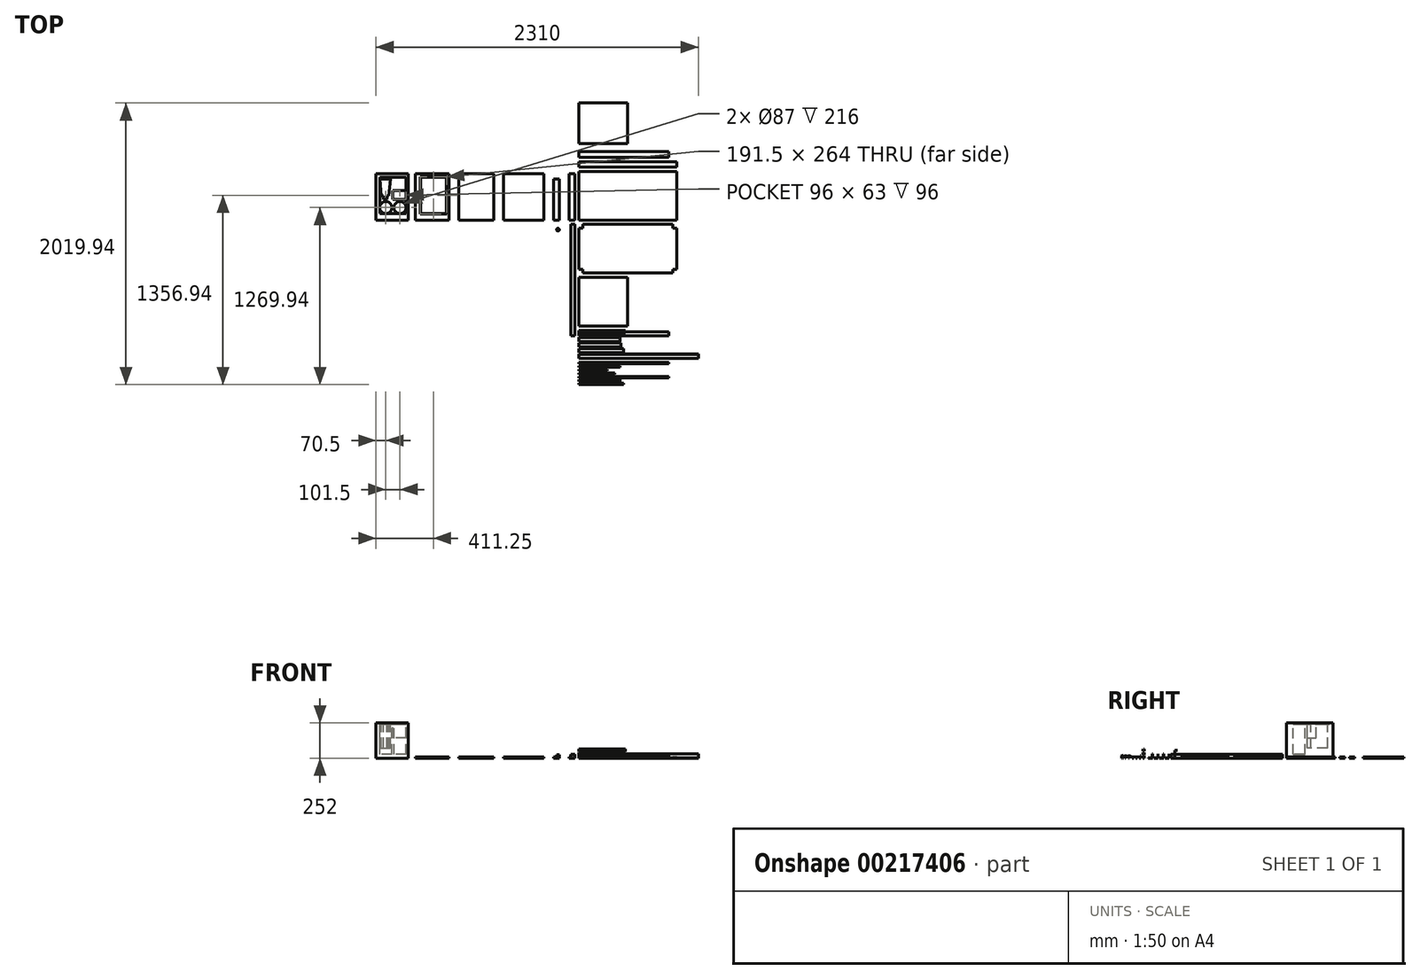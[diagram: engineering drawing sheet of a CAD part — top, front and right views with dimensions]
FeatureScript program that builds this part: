
annotation { "Feature Type Name" : "Feature", "Feature Type Description" : "" }
export const myFeature = defineFeature(function(context is Context, id is Id, definition is map)
    precondition{}
    {
        {
            assignVariable(context, id + "F0", {"name" : "length", "anyValue" : 700});
        }
        {
            assignVariable(context, id + "F1", {"name" : "width", "anyValue" : 350});
        }
        {
            assignVariable(context, id + "F2", {"name" : "height", "anyValue" : 800});
        }
        {
            assignVariable(context, id + "F3", {"name" : "panelW", "anyValue" : 8});
        }
        {
            assignVariable(context, id + "F4", {"name" : "postW", "anyValue" : 28});
        }
        {
            assignVariable(context, id + "F5", {"name" : "shelfH", "anyValue" : 40});
        }
        {
            assignVariable(context, id + "F6", {"name" : "profileW", "anyValue" : 1.5});
        }
        {
            assignVariable(context, id + "F7", {"name" : "topH", "anyValue" : 290});
        }
        {
            var Q0;
            Q0=qCreatedBy(makeId("Top.planeOp"),FACE);
            var sketch = newSketch(context, id + "F8", { "sketchPlane" : qUnion([Q0])});
            skLineSegment(sketch, "E0.bottom", {"start": v(0, 0) * mm, "end": v(700, 0) * mm});
            skLineSegment(sketch, "E0.top", {"start": v(0, 350) * mm, "end": v(700, 350) * mm});
            skLineSegment(sketch, "E0.left", {"start": v(0, 0) * mm, "end": v(0, 350) * mm});
            skLineSegment(sketch, "E0.right", {"start": v(700, 0) * mm, "end": v(700, 350) * mm});
            skLineSegment(sketch, "E1.bottom", {"start": v(0, 380) * mm, "end": v(700, 380) * mm});
            skLineSegment(sketch, "E1.top", {"start": v(0, 420) * mm, "end": v(700, 420) * mm});
            skLineSegment(sketch, "E1.left", {"start": v(0, 380) * mm, "end": v(0, 420) * mm});
            skLineSegment(sketch, "E1.right", {"start": v(700, 380) * mm, "end": v(700, 420) * mm});
            skLineSegment(sketch, "E2.bottom", {"start": v(-30, 0) * mm, "end": v(-70, 0) * mm});
            skLineSegment(sketch, "E2.top", {"start": v(-30, 334) * mm, "end": v(-70, 334) * mm});
            skLineSegment(sketch, "E2.left", {"start": v(-30, 0) * mm, "end": v(-30, 334) * mm});
            skLineSegment(sketch, "E2.right", {"start": v(-70, 0) * mm, "end": v(-70, 334) * mm});
            skLineSegment(sketch, "E3.bottom", {"start": v(0, 450) * mm, "end": v(644, 450) * mm});
            skLineSegment(sketch, "E3.top", {"start": v(0, 490) * mm, "end": v(644, 490) * mm});
            skLineSegment(sketch, "E3.left", {"start": v(0, 450) * mm, "end": v(0, 490) * mm});
            skLineSegment(sketch, "E3.right", {"start": v(644, 450) * mm, "end": v(644, 490) * mm});
            skLineSegment(sketch, "E4.bottom", {"start": v(-140, 0) * mm, "end": v(-180, 0) * mm});
            skLineSegment(sketch, "E4.top", {"start": v(-140, 294) * mm, "end": v(-180, 294) * mm});
            skLineSegment(sketch, "E4.left", {"start": v(-140, 0) * mm, "end": v(-140, 294) * mm});
            skLineSegment(sketch, "E4.right", {"start": v(-180, 0) * mm, "end": v(-180, 294) * mm});
            skLineSegment(sketch, "E5.bottom", {"start": v(28, -30) * mm, "end": v(672, -30) * mm});
            skLineSegment(sketch, "E5.top", {"start": v(28, -380) * mm, "end": v(672, -380) * mm});
            skLineSegment(sketch, "E5.left", {"start": v(0, -58) * mm, "end": v(0, -352) * mm});
            skLineSegment(sketch, "E5.right", {"start": v(700, -58) * mm, "end": v(700, -352) * mm});
            skLineSegment(sketch, "E6", {"start": v(0, -58) * mm, "end": v(28, -58) * mm});
            skLineSegment(sketch, "E7", {"start": v(28, -58) * mm, "end": v(28, -30) * mm});
            skLineSegment(sketch, "E8", {"start": v(350, -30) * mm, "end": v(350, -380) * mm, "construction": true});
            skLineSegment(sketch, "E9", {"start": v(0, -205) * mm, "end": v(700, -205) * mm, "construction": true});
            skPoint(sketch, "E10.orphan", {"position": v(0, -30) * mm});
            skLineSegment(sketch, "E11.MirrorCS", {"start": v(700, -58) * mm, "end": v(672, -58) * mm});
            skLineSegment(sketch, "E12.MirrorCS", {"start": v(672, -58) * mm, "end": v(672, -30) * mm});
            skPoint(sketch, "E13.MirrorP", {"position": v(700, -30) * mm});
            skLineSegment(sketch, "E14.MirrorCS", {"start": v(0, -352) * mm, "end": v(28, -352) * mm});
            skLineSegment(sketch, "E15.MirrorCS", {"start": v(28, -352) * mm, "end": v(28, -380) * mm});
            skLineSegment(sketch, "E16.MirrorCS", {"start": v(672, -352) * mm, "end": v(672, -380) * mm});
            skLineSegment(sketch, "E17.MirrorCS", {"start": v(700, -352) * mm, "end": v(672, -352) * mm});
            skPoint(sketch, "E18.orphan", {"position": v(700, -380) * mm});
            skPoint(sketch, "E19.orphan", {"position": v(0, -380) * mm});
            skPoint(sketch, "E20.oppositeSnap0", {"position": v(-50, 334) * mm});
            skLineSegment(sketch, "E20.bottom", {"start": v(-250, 0) * mm, "end": v(-540, 0) * mm});
            skLineSegment(sketch, "E20.top", {"start": v(-250, 334) * mm, "end": v(-540, 334) * mm});
            skLineSegment(sketch, "E20.left", {"start": v(-250, 0) * mm, "end": v(-250, 334) * mm});
            skLineSegment(sketch, "E20.right", {"start": v(-540, 0) * mm, "end": v(-540, 334) * mm});
            skLineSegment(sketch, "E21.bottom", {"start": v(0, 550) * mm, "end": v(348.5, 550) * mm});
            skLineSegment(sketch, "E21.top", {"start": v(0, 840) * mm, "end": v(348.5, 840) * mm});
            skLineSegment(sketch, "E21.left", {"start": v(0, 550) * mm, "end": v(0, 840) * mm});
            skLineSegment(sketch, "E21.right", {"start": v(348.5, 550) * mm, "end": v(348.5, 840) * mm});
            skLineSegment(sketch, "E22.bottom", {"start": v(0, -410) * mm, "end": v(348.5, -410) * mm});
            skLineSegment(sketch, "E22.top", {"start": v(0, -760) * mm, "end": v(348.5, -760) * mm});
            skLineSegment(sketch, "E22.left", {"start": v(0, -410) * mm, "end": v(0, -760) * mm});
            skLineSegment(sketch, "E22.right", {"start": v(348.5, -410) * mm, "end": v(348.5, -760) * mm});
            skLineSegment(sketch, "E23.bottom", {"start": v(-610, 0) * mm, "end": v(-862, 0) * mm});
            skLineSegment(sketch, "E23.top", {"start": v(-610, 334) * mm, "end": v(-862, 334) * mm});
            skLineSegment(sketch, "E23.left", {"start": v(-610, 0) * mm, "end": v(-610, 334) * mm});
            skLineSegment(sketch, "E23.right", {"start": v(-862, 0) * mm, "end": v(-862, 334) * mm});
            skLineSegment(sketch, "E24.bottom", {"start": v(-932, 0) * mm, "end": v(-1172, 0) * mm});
            skLineSegment(sketch, "E24.top", {"start": v(-932, 334) * mm, "end": v(-1172, 334) * mm});
            skLineSegment(sketch, "E24.left", {"start": v(-932, 0) * mm, "end": v(-932, 334) * mm});
            skLineSegment(sketch, "E24.right", {"start": v(-1172, 0) * mm, "end": v(-1172, 334) * mm});
            skLineSegment(sketch, "E25.bottom", {"start": v(-947, 45) * mm, "end": v(-1138.5, 45) * mm});
            skLineSegment(sketch, "E25.top", {"start": v(-947, 309) * mm, "end": v(-1138.5, 309) * mm});
            skLineSegment(sketch, "E25.left", {"start": v(-947, 45) * mm, "end": v(-947, 309) * mm});
            skLineSegment(sketch, "E25.right", {"start": v(-1138.5, 45) * mm, "end": v(-1138.5, 309) * mm});
            skLineSegment(sketch, "E26.bottom", {"start": v(-1135.5, 306) * mm, "end": v(-950, 306) * mm});
            skLineSegment(sketch, "E26.top", {"start": v(-1135.5, 48) * mm, "end": v(-950, 48) * mm});
            skLineSegment(sketch, "E26.left", {"start": v(-1135.5, 306) * mm, "end": v(-1135.5, 48) * mm});
            skLineSegment(sketch, "E26.right", {"start": v(-950, 306) * mm, "end": v(-950, 48) * mm});
            skSolve(sketch);
        }
        {
            var Q0;
            Q0 = qSketchRegion(id + "F8", true);
            extrude(context, id + "F9", {"entities" : qUnion([Q0]), "depth" : (getVariable(context, 'panelW')) * mm});
        }
        {
            var Q0;
            Q0=qCreatedBy(makeId("Right.planeOp"),FACE);
            var sketch = newSketch(context, id + "F10", { "sketchPlane" : qUnion([Q0])});
            skLineSegment(sketch, "E27", {"start": v(-800, 0) * mm, "end": v(-800, 30) * mm});
            skLineSegment(sketch, "E28", {"start": v(-800, 30) * mm, "end": v(-801.5, 30) * mm});
            skLineSegment(sketch, "E29", {"start": v(-801.5, 30) * mm, "end": v(-801.5, 1.5) * mm});
            skLineSegment(sketch, "E30", {"start": v(-801.5, 1.5) * mm, "end": v(-830, 1.5) * mm});
            skLineSegment(sketch, "E31", {"start": v(-830, 1.5) * mm, "end": v(-830, 0) * mm});
            skLineSegment(sketch, "E32", {"start": v(-830, 0) * mm, "end": v(-800, 0) * mm});
            skLineSegment(sketch, "E33.1.0.0", {"start": v(-870, 0) * mm, "end": v(-840, 0) * mm});
            skLineSegment(sketch, "E33.1.0.1", {"start": v(-840, 0) * mm, "end": v(-840, 30) * mm});
            skLineSegment(sketch, "E33.1.0.2", {"start": v(-841.5, 1.5) * mm, "end": v(-870, 1.5) * mm});
            skLineSegment(sketch, "E33.1.0.3", {"start": v(-841.5, 30) * mm, "end": v(-841.5, 1.5) * mm});
            skLineSegment(sketch, "E33.1.0.4", {"start": v(-840, 30) * mm, "end": v(-841.5, 30) * mm});
            skLineSegment(sketch, "E33.1.0.5", {"start": v(-870, 1.5) * mm, "end": v(-870, 0) * mm});
            skLineSegment(sketch, "E33.2.0.0", {"start": v(-910, 0) * mm, "end": v(-880, 0) * mm});
            skLineSegment(sketch, "E33.2.0.1", {"start": v(-880, 0) * mm, "end": v(-880, 30) * mm});
            skLineSegment(sketch, "E33.2.0.2", {"start": v(-881.5, 1.5) * mm, "end": v(-910, 1.5) * mm});
            skLineSegment(sketch, "E33.2.0.3", {"start": v(-881.5, 30) * mm, "end": v(-881.5, 1.5) * mm});
            skLineSegment(sketch, "E33.2.0.4", {"start": v(-880, 30) * mm, "end": v(-881.5, 30) * mm});
            skLineSegment(sketch, "E33.2.0.5", {"start": v(-910, 1.5) * mm, "end": v(-910, 0) * mm});
            skLineSegment(sketch, "E33.3.0.0", {"start": v(-950, 0) * mm, "end": v(-920, 0) * mm});
            skLineSegment(sketch, "E33.3.0.1", {"start": v(-920, 0) * mm, "end": v(-920, 30) * mm});
            skLineSegment(sketch, "E33.3.0.2", {"start": v(-921.5, 1.5) * mm, "end": v(-950, 1.5) * mm});
            skLineSegment(sketch, "E33.3.0.3", {"start": v(-921.5, 30) * mm, "end": v(-921.5, 1.5) * mm});
            skLineSegment(sketch, "E33.3.0.4", {"start": v(-920, 30) * mm, "end": v(-921.5, 30) * mm});
            skLineSegment(sketch, "E33.3.0.5", {"start": v(-950, 1.5) * mm, "end": v(-950, 0) * mm});
            skLineSegment(sketch, "E33.4.0.0", {"start": v(-990, 0) * mm, "end": v(-960, 0) * mm});
            skLineSegment(sketch, "E33.4.0.1", {"start": v(-960, 0) * mm, "end": v(-960, 30) * mm});
            skLineSegment(sketch, "E33.4.0.2", {"start": v(-961.5, 1.5) * mm, "end": v(-990, 1.5) * mm});
            skLineSegment(sketch, "E33.4.0.3", {"start": v(-961.5, 30) * mm, "end": v(-961.5, 1.5) * mm});
            skLineSegment(sketch, "E33.4.0.4", {"start": v(-960, 30) * mm, "end": v(-961.5, 30) * mm});
            skLineSegment(sketch, "E33.4.0.5", {"start": v(-990, 1.5) * mm, "end": v(-990, 0) * mm});
            skLineSegment(sketch, "E33.direction1", {"start": v(-830, 0) * mm, "end": v(-870, 0) * mm, "construction": true});
            skLineSegment(sketch, "E34.direction1", {"start": v(-830, 0) * mm, "end": v(-805, 0) * mm, "construction": true});
            skLineSegment(sketch, "E35", {"start": v(-790.1, 46.14) * mm, "end": v(-790.1, 66.14) * mm});
            skLineSegment(sketch, "E36", {"start": v(-790.1, 66.14) * mm, "end": v(-791.6, 66.14) * mm});
            skLineSegment(sketch, "E37", {"start": v(-791.6, 66.14) * mm, "end": v(-791.6, 47.64) * mm});
            skLineSegment(sketch, "E38", {"start": v(-791.6, 47.64) * mm, "end": v(-810.1, 47.64) * mm});
            skLineSegment(sketch, "E39", {"start": v(-810.1, 47.64) * mm, "end": v(-810.1, 46.14) * mm});
            skLineSegment(sketch, "E40", {"start": v(-810.1, 46.14) * mm, "end": v(-790.1, 46.14) * mm});
            skSolve(sketch);
        }
        {
            var Q0;
            Q0=makeQuery(id+"F10.imprint","IMPRINT",FACE,{"disambiguationData":[TD([[makeQuery(id+"F10.imprint","IMPRINT",EDGE,{"derivedFrom":sQuery(id+"F10.wireOp",EDGE,"E27")}),1.0]])]});
            extrude(context, id + "F11", {"entities" : qUnion([Q0]), "depth" : (getVariable(context, 'length') - 2 * getVariable(context, 'postW')) * mm});
        }
        {
            var Q0;
            Q0=makeQuery(id+"F10.imprint","IMPRINT",FACE,{"disambiguationData":[TD([[makeQuery(id+"F10.imprint","IMPRINT",EDGE,{"derivedFrom":sQuery(id+"F10.wireOp",EDGE,"E33.1.0.0")}),1.0]])]});
            extrude(context, id + "F12", {"entities" : qUnion([Q0]), "depth" : (getVariable(context, 'width') - 2 * getVariable(context, 'postW')) * mm});
        }
        {
            var Q0;
            Q0=makeQuery(id+"F10.imprint","IMPRINT",FACE,{"disambiguationData":[TD([[makeQuery(id+"F10.imprint","IMPRINT",EDGE,{"derivedFrom":sQuery(id+"F10.wireOp",EDGE,"E33.2.0.0")}),1.0]])]});
            extrude(context, id + "F13", {"entities" : qUnion([Q0]), "depth" : (getVariable(context, 'topH') + getVariable(context, 'panelW') + 2) * mm});
        }
        {
            var Q0;
            Q0=makeQuery(id+"F10.imprint","IMPRINT",FACE,{"disambiguationData":[TD([[makeQuery(id+"F10.imprint","IMPRINT",EDGE,{"derivedFrom":sQuery(id+"F10.wireOp",EDGE,"E33.3.0.0")}),1.0]])]});
            extrude(context, id + "F14", {"entities" : qUnion([Q0]), "depth" : (getVariable(context, 'length') / 2 - getVariable(context, 'postW') - getVariable(context, 'profileW')) * mm});
        }
        {
            var Q0;
            Q0=makeQuery(id+"F10.imprint","IMPRINT",FACE,{"disambiguationData":[TD([[makeQuery(id+"F10.imprint","IMPRINT",EDGE,{"derivedFrom":sQuery(id+"F10.wireOp",EDGE,"E33.4.0.0")}),1.0]])]});
            extrude(context, id + "F15", {"entities" : qUnion([Q0]), "depth" : (getVariable(context, 'height') + 2 * getVariable(context, 'panelW') + getVariable(context, 'shelfH')) * mm});
        }
        {
            var Q0;
            Q0=qCreatedBy(makeId("Right.planeOp"),FACE);
            var sketch = newSketch(context, id + "F16", { "sketchPlane" : qUnion([Q0])});
            skLineSegment(sketch, "E41", {"start": v(-1020, 0) * mm, "end": v(-1030, 0) * mm});
            skLineSegment(sketch, "E42", {"start": v(-1030, 0) * mm, "end": v(-1030, 16.5) * mm});
            skLineSegment(sketch, "E43", {"start": v(-1030, 16.5) * mm, "end": v(-1028.5, 16.5) * mm});
            skLineSegment(sketch, "E44", {"start": v(-1028.5, 16.5) * mm, "end": v(-1028.5, 1.5) * mm});
            skLineSegment(sketch, "E45", {"start": v(-1028.5, 1.5) * mm, "end": v(-1021.5, 1.5) * mm});
            skLineSegment(sketch, "E46", {"start": v(-1021.5, 1.5) * mm, "end": v(-1021.5, 16.5) * mm});
            skLineSegment(sketch, "E47", {"start": v(-1021.5, 16.5) * mm, "end": v(-1020, 16.5) * mm});
            skLineSegment(sketch, "E48", {"start": v(-1020, 16.5) * mm, "end": v(-1020, 0) * mm});
            skLineSegment(sketch, "E49.1.0.0", {"start": v(-1045, 0) * mm, "end": v(-1055, 0) * mm});
            skLineSegment(sketch, "E49.1.0.1", {"start": v(-1045, 16.5) * mm, "end": v(-1045, 0) * mm});
            skLineSegment(sketch, "E49.1.0.2", {"start": v(-1046.5, 16.5) * mm, "end": v(-1045, 16.5) * mm});
            skLineSegment(sketch, "E49.1.0.3", {"start": v(-1046.5, 1.5) * mm, "end": v(-1046.5, 16.5) * mm});
            skLineSegment(sketch, "E49.1.0.4", {"start": v(-1053.5, 1.5) * mm, "end": v(-1046.5, 1.5) * mm});
            skLineSegment(sketch, "E49.1.0.5", {"start": v(-1053.5, 16.5) * mm, "end": v(-1053.5, 1.5) * mm});
            skLineSegment(sketch, "E49.1.0.6", {"start": v(-1055, 0) * mm, "end": v(-1055, 16.5) * mm});
            skLineSegment(sketch, "E49.1.0.7", {"start": v(-1055, 16.5) * mm, "end": v(-1053.5, 16.5) * mm});
            skLineSegment(sketch, "E49.2.0.0", {"start": v(-1070, 0) * mm, "end": v(-1080, 0) * mm});
            skLineSegment(sketch, "E49.2.0.1", {"start": v(-1070, 16.5) * mm, "end": v(-1070, 0) * mm});
            skLineSegment(sketch, "E49.2.0.2", {"start": v(-1071.5, 16.5) * mm, "end": v(-1070, 16.5) * mm});
            skLineSegment(sketch, "E49.2.0.3", {"start": v(-1071.5, 1.5) * mm, "end": v(-1071.5, 16.5) * mm});
            skLineSegment(sketch, "E49.2.0.4", {"start": v(-1078.5, 1.5) * mm, "end": v(-1071.5, 1.5) * mm});
            skLineSegment(sketch, "E49.2.0.5", {"start": v(-1078.5, 16.5) * mm, "end": v(-1078.5, 1.5) * mm});
            skLineSegment(sketch, "E49.2.0.6", {"start": v(-1080, 0) * mm, "end": v(-1080, 16.5) * mm});
            skLineSegment(sketch, "E49.2.0.7", {"start": v(-1080, 16.5) * mm, "end": v(-1078.5, 16.5) * mm});
            skLineSegment(sketch, "E49.3.0.0", {"start": v(-1095, 0) * mm, "end": v(-1105, 0) * mm});
            skLineSegment(sketch, "E49.3.0.1", {"start": v(-1095, 16.5) * mm, "end": v(-1095, 0) * mm});
            skLineSegment(sketch, "E49.3.0.2", {"start": v(-1096.5, 16.5) * mm, "end": v(-1095, 16.5) * mm});
            skLineSegment(sketch, "E49.3.0.3", {"start": v(-1096.5, 1.5) * mm, "end": v(-1096.5, 16.5) * mm});
            skLineSegment(sketch, "E49.3.0.4", {"start": v(-1103.5, 1.5) * mm, "end": v(-1096.5, 1.5) * mm});
            skLineSegment(sketch, "E49.3.0.5", {"start": v(-1103.5, 16.5) * mm, "end": v(-1103.5, 1.5) * mm});
            skLineSegment(sketch, "E49.3.0.6", {"start": v(-1105, 0) * mm, "end": v(-1105, 16.5) * mm});
            skLineSegment(sketch, "E49.3.0.7", {"start": v(-1105, 16.5) * mm, "end": v(-1103.5, 16.5) * mm});
            skLineSegment(sketch, "E49.direction1", {"start": v(-1030, 0) * mm, "end": v(-1055, 0) * mm, "construction": true});
            skLineSegment(sketch, "E50.0.1.0", {"start": v(-1020, 41.5) * mm, "end": v(-1020, 25) * mm});
            skLineSegment(sketch, "E50.0.1.1", {"start": v(-1020, 25) * mm, "end": v(-1030, 25) * mm});
            skLineSegment(sketch, "E50.0.1.2", {"start": v(-1021.5, 26.5) * mm, "end": v(-1021.5, 41.5) * mm});
            skLineSegment(sketch, "E50.0.1.3", {"start": v(-1028.5, 26.5) * mm, "end": v(-1021.5, 26.5) * mm});
            skLineSegment(sketch, "E50.0.1.4", {"start": v(-1028.5, 41.5) * mm, "end": v(-1028.5, 26.5) * mm});
            skLineSegment(sketch, "E50.0.1.5", {"start": v(-1030, 25) * mm, "end": v(-1030, 41.5) * mm});
            skLineSegment(sketch, "E50.0.1.6", {"start": v(-1030, 41.5) * mm, "end": v(-1028.5, 41.5) * mm});
            skLineSegment(sketch, "E50.0.1.7", {"start": v(-1021.5, 41.5) * mm, "end": v(-1020, 41.5) * mm});
            skLineSegment(sketch, "E50.0.2.0", {"start": v(-1020, 66.5) * mm, "end": v(-1020, 50) * mm});
            skLineSegment(sketch, "E50.0.2.1", {"start": v(-1020, 50) * mm, "end": v(-1030, 50) * mm});
            skLineSegment(sketch, "E50.0.2.2", {"start": v(-1021.5, 51.5) * mm, "end": v(-1021.5, 66.5) * mm});
            skLineSegment(sketch, "E50.0.2.3", {"start": v(-1028.5, 51.5) * mm, "end": v(-1021.5, 51.5) * mm});
            skLineSegment(sketch, "E50.0.2.4", {"start": v(-1028.5, 66.5) * mm, "end": v(-1028.5, 51.5) * mm});
            skLineSegment(sketch, "E50.0.2.5", {"start": v(-1030, 50) * mm, "end": v(-1030, 66.5) * mm});
            skLineSegment(sketch, "E50.0.2.6", {"start": v(-1030, 66.5) * mm, "end": v(-1028.5, 66.5) * mm});
            skLineSegment(sketch, "E50.0.2.7", {"start": v(-1021.5, 66.5) * mm, "end": v(-1020, 66.5) * mm});
            skLineSegment(sketch, "E50.direction1", {"start": v(-1020, 0) * mm, "end": v(-995, 0) * mm, "construction": true});
            skLineSegment(sketch, "E50.direction2", {"start": v(-1020, 0) * mm, "end": v(-1020, 25) * mm, "construction": true});
            skSolve(sketch);
        }
        {
            var Q0;
            Q0=makeQuery(id+"F16.imprint","IMPRINT",FACE,{"disambiguationData":[TD([[makeQuery(id+"F16.imprint","IMPRINT",EDGE,{"derivedFrom":sQuery(id+"F16.wireOp",EDGE,"E41")}),-1.0]])]});
            extrude(context, id + "F17", {"entities" : qUnion([Q0]), "depth" : (getVariable(context, 'length') - 2 * getVariable(context, 'postW')) * mm});
        }
        {
            var Q0;
            Q0=makeQuery(id+"F16.imprint","IMPRINT",FACE,{"disambiguationData":[TD([[makeQuery(id+"F16.imprint","IMPRINT",EDGE,{"derivedFrom":sQuery(id+"F16.wireOp",EDGE,"E49.1.0.0")}),-1.0]])]});
            extrude(context, id + "F18", {"entities" : qUnion([Q0]), "depth" : (getVariable(context, 'width') - 2 * getVariable(context, 'postW')) * mm});
        }
        {
            var Q0;
            Q0=makeQuery(id+"F16.imprint","IMPRINT",FACE,{"disambiguationData":[TD([[makeQuery(id+"F16.imprint","IMPRINT",EDGE,{"derivedFrom":sQuery(id+"F16.wireOp",EDGE,"E49.3.0.0")}),-1.0]])]});
            extrude(context, id + "F19", {"entities" : qUnion([Q0]), "depth" : (getVariable(context, 'topH') + getVariable(context, 'panelW') - getVariable(context, 'postW') - 15) * mm});
        }
        {
            var Q0;
            Q0=makeQuery(id+"F16.imprint","IMPRINT",FACE,{"disambiguationData":[TD([[makeQuery(id+"F16.imprint","IMPRINT",EDGE,{"derivedFrom":sQuery(id+"F16.wireOp",EDGE,"E49.2.0.0")}),-1.0]])]});
            extrude(context, id + "F20", {"entities" : qUnion([Q0]), "depth" : (172 + 2 * 15) * mm});
        }
        {
            var Q0;
            Q0=qCreatedBy(makeId("Right.planeOp"),FACE);
            var sketch = newSketch(context, id + "F21", { "sketchPlane" : qUnion([Q0])});
            skLineSegment(sketch, "E51", {"start": v(-1119.94, 0) * mm, "end": v(-1119.94, 20.5) * mm});
            skLineSegment(sketch, "E52", {"start": v(-1119.94, 20.5) * mm, "end": v(-1123.27, 17.17) * mm});
            skLineSegment(sketch, "E53", {"start": v(-1123.27, 17.17) * mm, "end": v(-1126.6, 20.5) * mm});
            skLineSegment(sketch, "E54", {"start": v(-1126.6, 20.5) * mm, "end": v(-1129.94, 17.17) * mm});
            skLineSegment(sketch, "E55", {"start": v(-1129.94, 17.17) * mm, "end": v(-1129.94, 0) * mm});
            skLineSegment(sketch, "E56", {"start": v(-1129.94, 0) * mm, "end": v(-1128.44, 0) * mm});
            skLineSegment(sketch, "E57", {"start": v(-1128.44, 0) * mm, "end": v(-1128.44, 15) * mm});
            skLineSegment(sketch, "E58", {"start": v(-1128.44, 15) * mm, "end": v(-1121.44, 15) * mm});
            skLineSegment(sketch, "E59", {"start": v(-1121.44, 15) * mm, "end": v(-1121.44, 0) * mm});
            skLineSegment(sketch, "E60", {"start": v(-1121.44, 0) * mm, "end": v(-1119.94, 0) * mm});
            skLineSegment(sketch, "E61.1.0.0", {"start": v(-1154.94, 0) * mm, "end": v(-1153.44, 0) * mm});
            skLineSegment(sketch, "E61.1.0.1", {"start": v(-1154.94, 17.17) * mm, "end": v(-1154.94, 0) * mm});
            skLineSegment(sketch, "E61.1.0.2", {"start": v(-1153.44, 0) * mm, "end": v(-1153.44, 15) * mm});
            skLineSegment(sketch, "E61.1.0.3", {"start": v(-1153.44, 15) * mm, "end": v(-1146.44, 15) * mm});
            skLineSegment(sketch, "E61.1.0.4", {"start": v(-1146.44, 15) * mm, "end": v(-1146.44, 0) * mm});
            skLineSegment(sketch, "E61.1.0.5", {"start": v(-1146.44, 0) * mm, "end": v(-1144.94, 0) * mm});
            skLineSegment(sketch, "E61.1.0.6", {"start": v(-1144.94, 0) * mm, "end": v(-1144.94, 20.5) * mm});
            skLineSegment(sketch, "E61.1.0.7", {"start": v(-1144.94, 20.5) * mm, "end": v(-1148.27, 17.17) * mm});
            skLineSegment(sketch, "E61.1.0.8", {"start": v(-1148.27, 17.17) * mm, "end": v(-1151.6, 20.5) * mm});
            skLineSegment(sketch, "E61.1.0.9", {"start": v(-1151.6, 20.5) * mm, "end": v(-1154.94, 17.17) * mm});
            skLineSegment(sketch, "E61.2.0.0", {"start": v(-1179.94, 0) * mm, "end": v(-1178.44, 0) * mm});
            skLineSegment(sketch, "E61.2.0.1", {"start": v(-1179.94, 17.17) * mm, "end": v(-1179.94, 0) * mm});
            skLineSegment(sketch, "E61.2.0.2", {"start": v(-1178.44, 0) * mm, "end": v(-1178.44, 15) * mm});
            skLineSegment(sketch, "E61.2.0.3", {"start": v(-1178.44, 15) * mm, "end": v(-1171.44, 15) * mm});
            skLineSegment(sketch, "E61.2.0.4", {"start": v(-1171.44, 15) * mm, "end": v(-1171.44, 0) * mm});
            skLineSegment(sketch, "E61.2.0.5", {"start": v(-1171.44, 0) * mm, "end": v(-1169.94, 0) * mm});
            skLineSegment(sketch, "E61.2.0.6", {"start": v(-1169.94, 0) * mm, "end": v(-1169.94, 20.5) * mm});
            skLineSegment(sketch, "E61.2.0.7", {"start": v(-1169.94, 20.5) * mm, "end": v(-1173.27, 17.17) * mm});
            skLineSegment(sketch, "E61.2.0.8", {"start": v(-1173.27, 17.17) * mm, "end": v(-1176.6, 20.5) * mm});
            skLineSegment(sketch, "E61.2.0.9", {"start": v(-1176.6, 20.5) * mm, "end": v(-1179.94, 17.17) * mm});
            skLineSegment(sketch, "E61.direction1", {"start": v(-1129.94, 0) * mm, "end": v(-1154.94, 0) * mm, "construction": true});
            skSolve(sketch);
        }
        {
            var Q0;
            Q0=makeQuery(id+"F21.imprint","IMPRINT",FACE,{"disambiguationData":[TD([[makeQuery(id+"F21.imprint","IMPRINT",EDGE,{"derivedFrom":sQuery(id+"F21.wireOp",EDGE,"E51")}),1.0]])]});
            extrude(context, id + "F22", {"entities" : qUnion([Q0]), "depth" : (getVariable(context, 'length') - 2 * getVariable(context, 'postW')) * mm});
        }
        {
            var Q0;
            Q0=makeQuery(id+"F21.imprint","IMPRINT",FACE,{"disambiguationData":[TD([[makeQuery(id+"F21.imprint","IMPRINT",EDGE,{"derivedFrom":sQuery(id+"F21.wireOp",EDGE,"E61.1.0.0")}),1.0]])]});
            extrude(context, id + "F23", {"entities" : qUnion([Q0]), "depth" : (getVariable(context, 'width') - 2 * getVariable(context, 'postW')) * mm});
        }
        {
            var Q0;
            Q0=makeQuery(id+"F21.imprint","IMPRINT",FACE,{"disambiguationData":[TD([[makeQuery(id+"F21.imprint","IMPRINT",EDGE,{"derivedFrom":sQuery(id+"F21.wireOp",EDGE,"E61.2.0.0")}),1.0]])]});
            extrude(context, id + "F24", {"entities" : qUnion([Q0]), "depth" : (getVariable(context, 'length') / 2 - getVariable(context, 'postW') - getVariable(context, 'profileW')) * mm});
        }
        {
            var Q0;
            Q0=qCreatedBy(makeId("Top.planeOp"),FACE);
            var sketch = newSketch(context, id + "F25", { "sketchPlane" : qUnion([Q0])});
            skLineSegment(sketch, "E62.bottom", {"start": v(-30, -30) * mm, "end": v(-58, -30) * mm});
            skLineSegment(sketch, "E62.top", {"start": v(-30, -830) * mm, "end": v(-58, -830) * mm});
            skLineSegment(sketch, "E62.left", {"start": v(-30, -30) * mm, "end": v(-30, -830) * mm});
            skLineSegment(sketch, "E62.right", {"start": v(-58, -30) * mm, "end": v(-58, -830) * mm});
            skSolve(sketch);
        }
        {
            var Q0;
            Q0=makeQuery(id+"F25.imprint","IMPRINT",FACE,{"disambiguationData":[TD([[makeQuery(id+"F25.imprint","IMPRINT",EDGE,{"derivedFrom":sQuery(id+"F25.wireOp",EDGE,"E62.bottom")}),1.0]])]});
            extrude(context, id + "F26", {"entities" : qUnion([Q0]), "depth" : (getVariable(context, 'postW')) * mm});
        }
        {
            var Q0;
            Q0=qCreatedBy(makeId("Top.planeOp"),FACE);
            var sketch = newSketch(context, id + "F27", { "sketchPlane" : qUnion([Q0])});
            skCircle(sketch, "E63", {"center": v(-150.24, -68.61) * mm, "radius": 10 * mm});
            skSolve(sketch);
        }
        {
            var Q0;
            Q0 = qSketchRegion(id + "F27", true);
            extrude(context, id + "F28", {"entities" : qUnion([Q0]), "depth" : 25 * mm});
        }
        {
            var Q0;
            Q0=makeQuery(id+"F8.imprint","IMPRINT",FACE,{"disambiguationData":[TD([[makeQuery(id+"F8.imprint","IMPRINT",EDGE,{"derivedFrom":sQuery(id+"F8.wireOp",EDGE,"E26.bottom")}),-1.0]])]});
            extrude(context, id + "F29", {"entities" : qUnion([Q0]), "depth" : (getVariable(context, 'panelW')) * mm});
        }
        {
            var Q0;
            Q0=makeQuery(id+"F16.imprint","IMPRINT",FACE,{"disambiguationData":[TD([[makeQuery(id+"F16.imprint","IMPRINT",EDGE,{"derivedFrom":sQuery(id+"F16.wireOp",EDGE,"E50.0.1.0")}),-1.0]])]});
            extrude(context, id + "F30", {"entities" : qUnion([Q0]), "depth" : 255 * mm});
        }
        {
            var Q0;
            Q0=makeQuery(id+"F16.imprint","IMPRINT",FACE,{"disambiguationData":[TD([[makeQuery(id+"F16.imprint","IMPRINT",EDGE,{"derivedFrom":sQuery(id+"F16.wireOp",EDGE,"E50.0.2.0")}),-1.0]])]});
            extrude(context, id + "F31", {"entities" : qUnion([Q0]), "depth" : 166 * mm});
        }
        {
            var Q0;
            Q0=qCreatedBy(makeId("Top.planeOp"),FACE);
            var sketch = newSketch(context, id + "F32", { "sketchPlane" : qUnion([Q0])});
            skLineSegment(sketch, "E64.bottom", {"start": v(-1222, 0) * mm, "end": v(-1454, 0) * mm});
            skLineSegment(sketch, "E64.top", {"start": v(-1222, 334) * mm, "end": v(-1454, 334) * mm});
            skLineSegment(sketch, "E64.left", {"start": v(-1222, 0) * mm, "end": v(-1222, 334) * mm});
            skLineSegment(sketch, "E64.right", {"start": v(-1454, 0) * mm, "end": v(-1454, 334) * mm});
            skSolve(sketch);
        }
        {
            var Q0;
            Q0 = qSketchRegion(id + "F32", true);
            extrude(context, id + "F33", {"entities" : qUnion([Q0]), "depth" : 252 * mm});
        }
        {
            var Q0;
            Q0=makeQuery(id+"F10.imprint","IMPRINT",FACE,{"disambiguationData":[TD([[makeQuery(id+"F10.imprint","IMPRINT",EDGE,{"derivedFrom":sQuery(id+"F10.wireOp",EDGE,"E35")}),1.0]])]});
            extrude(context, id + "F34", {"entities" : qUnion([Q0]), "depth" : 334 * mm});
        }
        {
            var Q0;
            Q0=makeQuery(id+"F33.opExtrude","CAP_FACE",FACE,{"disambiguationData":[OSD([sQuery(id+"F32.wireOp",EDGE,"E64.bottom"),sQuery(id+"F32.wireOp",EDGE,"E64.top"),sQuery(id+"F32.wireOp",EDGE,"E64.left"),sQuery(id+"F32.wireOp",EDGE,"E64.right")])],"isStart":false});
            var sketch = newSketch(context, id + "F35", { "sketchPlane" : qUnion([Q0])});
            skLineSegment(sketch, "E65.bottom", {"start": v(-1427, 46.5) * mm, "end": v(-1238.5, 46.5) * mm});
            skLineSegment(sketch, "E65.top", {"start": v(-1427, 307.5) * mm, "end": v(-1238.5, 307.5) * mm});
            skLineSegment(sketch, "E65.left", {"start": v(-1427, 46.5) * mm, "end": v(-1427, 307.5) * mm});
            skLineSegment(sketch, "E65.right", {"start": v(-1238.5, 46.5) * mm, "end": v(-1238.5, 307.5) * mm});
            skSolve(sketch);
        }
        {
            var Q0;
            Q0 = qSketchRegion(id + "F35", true);
            extrude(context, id + "F36", {"entities" : qUnion([Q0]), "operationType" : NewBodyOperationType.REMOVE, "oppositeDirection" : true, "depth" : 10 * mm});
        }
        {
            var Q0;
            Q0=makeQuery(id+"F36.boolean.opBoolean","COPY",FACE,{"derivedFrom":makeQuery(id+"F36.opExtrude","CAP_FACE",FACE,{"disambiguationData":[OSD([sQuery(id+"F35.wireOp",EDGE,"E65.bottom"),sQuery(id+"F35.wireOp",EDGE,"E65.top"),sQuery(id+"F35.wireOp",EDGE,"E65.left"),sQuery(id+"F35.wireOp",EDGE,"E65.right")])],"isStart":false})});
            var sketch = newSketch(context, id + "F37", { "sketchPlane" : qUnion([Q0])});
            skCircle(sketch, "E66", {"center": v(-1282, 90) * mm, "radius": 43.5 * mm});
            skCircle(sketch, "E67", {"center": v(-1383.5, 90) * mm, "radius": 43.5 * mm});
            skSolve(sketch);
        }
        {
            var Q0;
            Q0 = qSketchRegion(id + "F37", true);
            extrude(context, id + "F38", {"entities" : qUnion([Q0]), "operationType" : NewBodyOperationType.REMOVE, "oppositeDirection" : true, "depth" : (108 * 2) * mm});
        }
        {
            var Q0;
            {var subQ0=sQuery(id+"F35.wireOp",EDGE,"E65.left");var subQ1=sQuery(id+"F35.wireOp",EDGE,"E65.top");var subQ2=sQuery(id+"F35.wireOp",EDGE,"E65.right");var subQ3=sQuery(id+"F35.wireOp",EDGE,"E65.bottom");var subQ4=makeQuery(id+"F36.boolean.opBoolean","COPY",FACE,{"derivedFrom":makeQuery(id+"F36.opExtrude","CAP_FACE",FACE,{"disambiguationData":[OSD([subQ3,subQ1,subQ0,subQ2])],"isStart":false})});Q0=makeQuery(id+"F38.boolean.opBoolean","SPLIT",FACE,{"disambiguationData":[TD([makeQuery(id+"F36.boolean.opBoolean","COPY",FACE,{"derivedFrom":makeQuery(id+"F36.opExtrude","SWEPT_FACE",FACE,{"disambiguationData":[OSD([subQ3])]})}),subQ4,makeQuery(id+"F36.boolean.opBoolean","COPY",FACE,{"derivedFrom":makeQuery(id+"F36.opExtrude","SWEPT_FACE",FACE,{"disambiguationData":[OSD([subQ1])]})}),makeQuery(id+"F36.boolean.opBoolean","COPY",FACE,{"derivedFrom":makeQuery(id+"F36.opExtrude","SWEPT_FACE",FACE,{"disambiguationData":[OSD([subQ0])]})}),makeQuery(id+"F36.boolean.opBoolean","COPY",FACE,{"derivedFrom":makeQuery(id+"F36.opExtrude","SWEPT_FACE",FACE,{"disambiguationData":[OSD([subQ2])]})}),makeQuery(id+"F38.opExtrude","SWEPT_FACE",FACE,{"disambiguationData":[OSD([sQuery(id+"F37.wireOp",EDGE,"E66")])]}),makeQuery(id+"F38.opExtrude","SWEPT_FACE",FACE,{"disambiguationData":[OSD([sQuery(id+"F37.wireOp",EDGE,"E67")])]})])],"derivedFrom":subQ4});}
            var sketch = newSketch(context, id + "F39", { "sketchPlane" : qUnion([Q0])});
            skLineSegment(sketch, "E68.bottom", {"start": v(-1238.5, 211.5) * mm, "end": v(-1334.5, 211.5) * mm});
            skLineSegment(sketch, "E68.top", {"start": v(-1238.5, 148.5) * mm, "end": v(-1334.5, 148.5) * mm});
            skLineSegment(sketch, "E68.left", {"start": v(-1238.5, 211.5) * mm, "end": v(-1238.5, 148.5) * mm});
            skLineSegment(sketch, "E68.right", {"start": v(-1334.5, 211.5) * mm, "end": v(-1334.5, 148.5) * mm});
            skSolve(sketch);
        }
        {
            var Q0;
            Q0 = qSketchRegion(id + "F39", true);
            extrude(context, id + "F40", {"entities" : qUnion([Q0]), "operationType" : NewBodyOperationType.REMOVE, "oppositeDirection" : true, "depth" : (48 * 2) * mm});
        }
        {
            var Q0;
            {var subQ0=sQuery(id+"F35.wireOp",EDGE,"E65.left");var subQ1=sQuery(id+"F35.wireOp",EDGE,"E65.top");var subQ2=sQuery(id+"F35.wireOp",EDGE,"E65.right");var subQ3=sQuery(id+"F35.wireOp",EDGE,"E65.bottom");var subQ4=makeQuery(id+"F36.boolean.opBoolean","COPY",FACE,{"derivedFrom":makeQuery(id+"F36.opExtrude","CAP_FACE",FACE,{"disambiguationData":[OSD([subQ3,subQ1,subQ0,subQ2])],"isStart":false})});Q0=makeQuery(id+"F38.boolean.opBoolean","SPLIT",FACE,{"disambiguationData":[TD([makeQuery(id+"F36.boolean.opBoolean","COPY",FACE,{"derivedFrom":makeQuery(id+"F36.opExtrude","SWEPT_FACE",FACE,{"disambiguationData":[OSD([subQ3])]})}),subQ4,makeQuery(id+"F36.boolean.opBoolean","COPY",FACE,{"derivedFrom":makeQuery(id+"F36.opExtrude","SWEPT_FACE",FACE,{"disambiguationData":[OSD([subQ1])]})}),makeQuery(id+"F36.boolean.opBoolean","COPY",FACE,{"derivedFrom":makeQuery(id+"F36.opExtrude","SWEPT_FACE",FACE,{"disambiguationData":[OSD([subQ0])]})}),makeQuery(id+"F36.boolean.opBoolean","COPY",FACE,{"derivedFrom":makeQuery(id+"F36.opExtrude","SWEPT_FACE",FACE,{"disambiguationData":[OSD([subQ2])]})}),makeQuery(id+"F38.opExtrude","SWEPT_FACE",FACE,{"disambiguationData":[OSD([sQuery(id+"F37.wireOp",EDGE,"E66")])]}),makeQuery(id+"F38.opExtrude","SWEPT_FACE",FACE,{"disambiguationData":[OSD([sQuery(id+"F37.wireOp",EDGE,"E67")])]})])],"derivedFrom":subQ4});}
            var sketch = newSketch(context, id + "F41", { "sketchPlane" : qUnion([Q0])});
            skLineSegment(sketch, "E69", {"start": v(-1389, 295.5) * mm, "end": v(-1427, 295.5) * mm});
            skLineSegment(sketch, "E70", {"start": v(-1427, 295.5) * mm, "end": v(-1416, 173.5) * mm});
            skLineSegment(sketch, "E71", {"start": v(-1416, 173.5) * mm, "end": v(-1401.5, 173.5) * mm});
            skLineSegment(sketch, "E72", {"start": v(-1401.5, 173.5) * mm, "end": v(-1401.5, 148.5) * mm});
            skLineSegment(sketch, "E73", {"start": v(-1401.5, 148.5) * mm, "end": v(-1389, 148.5) * mm});
            skLineSegment(sketch, "E74", {"start": v(-1389, 148.5) * mm, "end": v(-1389, 295.5) * mm, "construction": true});
            skLineSegment(sketch, "E75.MirrorCS", {"start": v(-1376.5, 148.5) * mm, "end": v(-1389, 148.5) * mm});
            skLineSegment(sketch, "E76.MirrorCS", {"start": v(-1376.5, 173.5) * mm, "end": v(-1376.5, 148.5) * mm});
            skLineSegment(sketch, "E77.MirrorCS", {"start": v(-1362, 173.5) * mm, "end": v(-1376.5, 173.5) * mm});
            skLineSegment(sketch, "E78.MirrorCS", {"start": v(-1351, 295.5) * mm, "end": v(-1362, 173.5) * mm});
            skLineSegment(sketch, "E79.MirrorCS", {"start": v(-1389, 295.5) * mm, "end": v(-1351, 295.5) * mm});
            skSolve(sketch);
        }
        {
            var Q0;
            Q0 = qSketchRegion(id + "F41", true);
            extrude(context, id + "F42", {"entities" : qUnion([Q0]), "operationType" : NewBodyOperationType.REMOVE, "oppositeDirection" : true, "depth" : 170 * mm});
        }
    });
